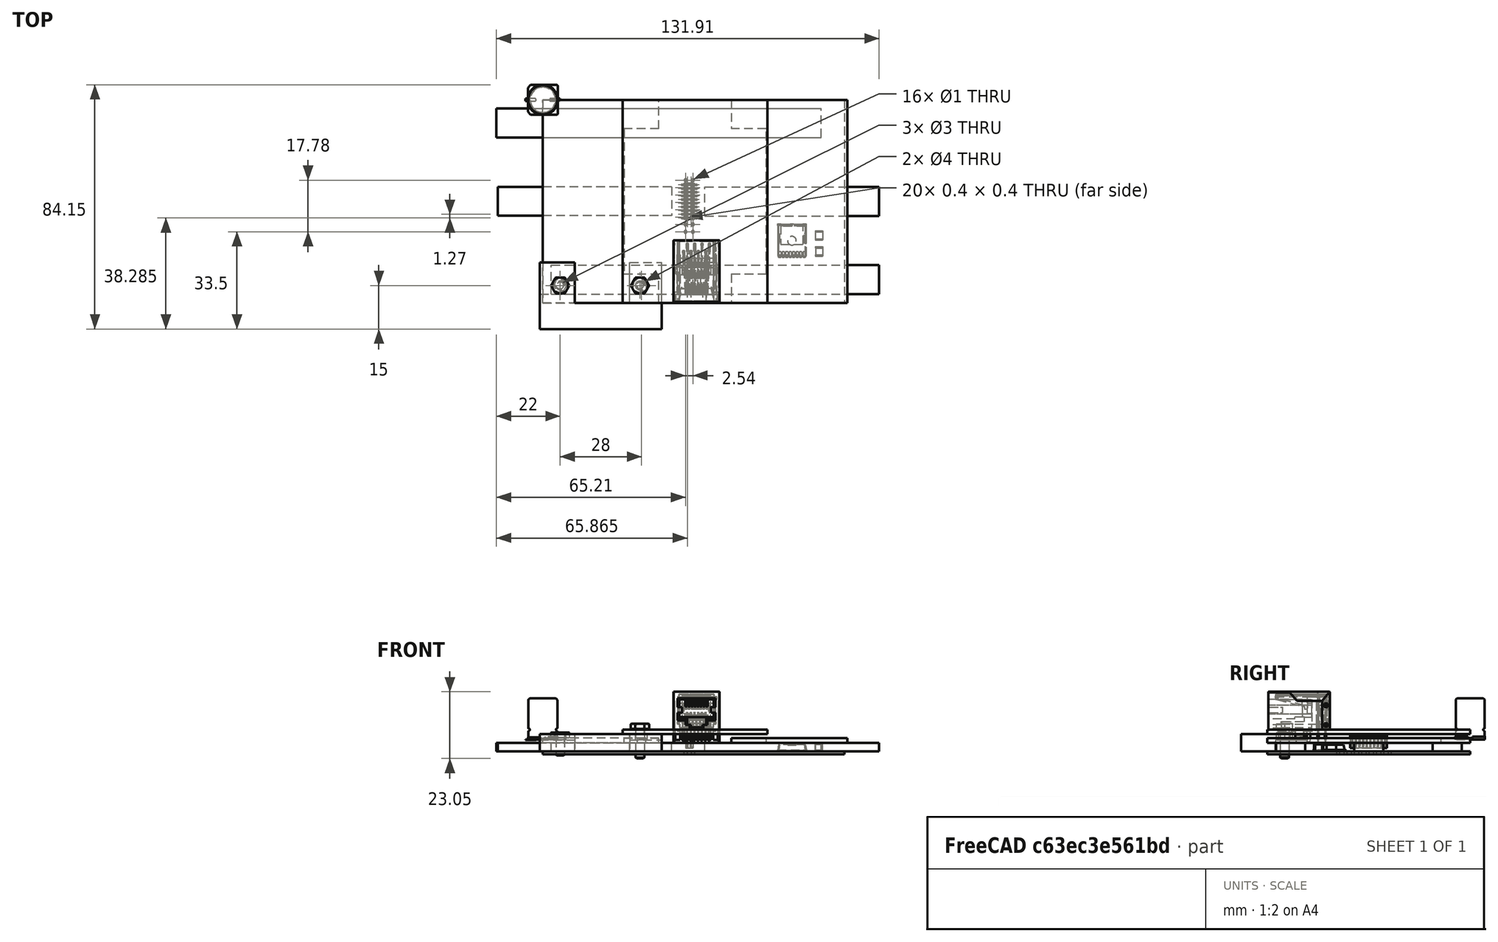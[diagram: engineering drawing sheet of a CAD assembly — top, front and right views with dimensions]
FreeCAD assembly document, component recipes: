
FREECAD ASSEMBLY — COMPONENT RECIPES ("Swiches")

This assembly document has 4 components, labeled P0..P3 below (a component is one placed body or linked part). 3 of them carry a construction recipe — the FreeCAD feature program that regenerates the part from scratch, quoted from this document or its linked companion documents; the rest are supplied as boundary geometry only. No exploded tour is included for this assembly.
COMPONENT P0 — geometry summary ("Switches"; no construction recipe available for this part):
  bounding box: 104.0 x 70.0 x 3.5 mm
  tessellated surface: 16,348 triangles
  volume: 10071 mm^3 (40% of its bounding box)
  symmetry: mirror-symmetric across its y mid-plane
COMPONENT P1 — recipe-attached ("Body", modeled in this document).
Construction recipe (the document's own serialized feature program — sketch geometry with constraints, then the solid features built on it; lengths are millimeters unless a unit is written):

FEATURE [Sketcher::SketchObject] Sketch
  FullyConstrained = true
  sketch-geometry (10):
    g0: LineSegment StartX=0 StartY=-70 StartZ=0 EndX=40 EndY=-70 EndZ=0
    g1: LineSegment StartX=40 StartY=-70 StartZ=0 EndX=40 EndY=-60 EndZ=0
    g2: LineSegment StartX=40 StartY=-10 StartZ=0 EndX=40 EndY=0 EndZ=0
    g3: LineSegment StartX=40 StartY=0 StartZ=0 EndX=0 EndY=0 EndZ=0
    g4: LineSegment StartX=40 StartY=-10 StartZ=0 EndX=28 EndY=-10 EndZ=0
    g5: LineSegment StartX=28 StartY=-60 StartZ=0 EndX=40 EndY=-60 EndZ=0
    g6: LineSegment StartX=0 StartY=0 StartZ=0 EndX=0 EndY=-70 EndZ=0
    g7: LineSegment StartX=28 StartY=-10 StartZ=0 EndX=28 EndY=-60 EndZ=0
    g8: Circle CenterX=6 CenterY=-64 CenterZ=0 NormalX=0 NormalY=0 NormalZ=1 AngleXU=0 Radius=1.5
    g9: Circle CenterX=34 CenterY=-64 CenterZ=0 NormalX=0 NormalY=0 NormalZ=1 AngleXU=0 Radius=1.5
  constraints (30):
    c: Coincident(g0,g1)
    c: Coincident(g5,g7)
    c: Coincident(g4,g7)
    c: Coincident(g4,g2)
    c: Coincident(g3,g2)
    c: Coincident(g6,g3)
    c: Coincident(g6,g0)
    c: Vertical(g6)
    c: Vertical(g7)
    c: Vertical(g1)
    c: Vertical(g2)
    c: Horizontal(g0)
    c: Horizontal(g3)
    c: Horizontal(g4)
    c: Horizontal(g5)
    c: Coincident(g1,g5)
    c: Equal(g4,g5)
    c: Equal(g2,g1)
    c: DistanceX(g3,g3) = 40
    c: DistanceY(g6,g6) = 70
    c: DistanceY(g2,g2) = 10
    c: DistanceX(g4,g4) = 12
    c: DistanceX(g3) = 0
    c: DistanceY(g3) = 0
    c: Diameter(g8) = 3
    c: DistanceY(g0,g8) = 6
    c: DistanceX(g0,g8) = 6
    c: DistanceY(g0,g9) = 6
    c: DistanceX(g9,g0) = 6
    c: Diameter(g9) = 3
FEATURE [PartDesign::Pad] Pad
  Direction = (1,1,1)
  Length = 1.6
  Length2 = 100
  Profile = -> Sketch
  Type = 0
FEATURE [PartDesign::Body] Body
  Group = -> [Sketch,Pad]
  Origin = -> Origin008
  Placement = pos=(0,0,3) rot=(0,0,1;0rad)
  Tip = -> Pad
COMPONENT P2 — recipe-attached ("Body001", modeled in this document).
Construction recipe (the document's own serialized feature program — sketch geometry with constraints, then the solid features built on it; lengths are millimeters unless a unit is written):

FEATURE [Sketcher::SketchObject] Sketch002
  FullyConstrained = true
  MapMode = 5
  Support = -> [XY_Plane009]
  sketch-geometry (5):
    g0: LineSegment StartX=10 StartY=0 StartZ=0 EndX=60 EndY=0 EndZ=0
    g1: LineSegment StartX=60 StartY=0 StartZ=0 EndX=60 EndY=-70 EndZ=0
    g2: LineSegment StartX=60 StartY=-70 StartZ=0 EndX=10 EndY=-70 EndZ=0
    g3: LineSegment StartX=10 StartY=-70 StartZ=0 EndX=10 EndY=0 EndZ=0
    g4: Circle CenterX=16 CenterY=-64 CenterZ=0 NormalX=0 NormalY=0 NormalZ=1 AngleXU=0 Radius=1.5
  constraints (15):
    c: Coincident(g0,g1)
    c: Coincident(g1,g2)
    c: Coincident(g2,g3)
    c: Coincident(g3,g0)
    c: Horizontal(g0)
    c: Horizontal(g2)
    c: Vertical(g1)
    c: Vertical(g3)
    c: Distance(g0) = 50
    c: Distance(g1) = 70
    c: DistanceX(g0,g-1) = -10
    c: DistanceY(g0,g-1) = 0
    c: DistanceY(g2,g4) = 6
    c: DistanceX(g2,g4) = 6
    c: Diameter(g4) = 3
FEATURE [PartDesign::Pad] Pad001
  Direction = (1,1,1)
  Length = 1.6
  Length2 = 100
  Profile = -> Sketch002
  Type = 0
FEATURE [PartDesign::Body] Body001
  Group = -> [Sketch002,Pad001]
  Origin = -> Origin009
  Placement = pos=(17.5,0,6) rot=(0,0,1;0rad)
  Tip = -> Pad001
COMPONENT P3 — recipe-attached ("Body002", modeled in this document).
Construction recipe (the document's own serialized feature program — sketch geometry with constraints, then the solid features built on it; lengths are millimeters unless a unit is written):

FEATURE [Sketcher::SketchObject] Sketch003
  FullyConstrained = true
  sketch-geometry (8):
    g0: LineSegment StartX=0 StartY=-70 StartZ=0 EndX=40 EndY=-70 EndZ=0
    g1: LineSegment StartX=40 StartY=-70 StartZ=0 EndX=40 EndY=-60 EndZ=0
    g2: LineSegment StartX=40 StartY=-10 StartZ=0 EndX=40 EndY=0 EndZ=0
    g3: LineSegment StartX=40 StartY=0 StartZ=0 EndX=0 EndY=0 EndZ=0
    g4: LineSegment StartX=40 StartY=-10 StartZ=0 EndX=28 EndY=-10 EndZ=0
    g5: LineSegment StartX=28 StartY=-60 StartZ=0 EndX=40 EndY=-60 EndZ=0
    g6: LineSegment StartX=0 StartY=0 StartZ=0 EndX=0 EndY=-70 EndZ=0
    g7: LineSegment StartX=28 StartY=-10 StartZ=0 EndX=28 EndY=-60 EndZ=0
  constraints (24):
    c: Coincident(g0,g1)
    c: Coincident(g5,g7)
    c: Coincident(g4,g7)
    c: Coincident(g4,g2)
    c: Coincident(g3,g2)
    c: Coincident(g6,g3)
    c: Coincident(g6,g0)
    c: Vertical(g6)
    c: Vertical(g7)
    c: Vertical(g1)
    c: Vertical(g2)
    c: Horizontal(g0)
    c: Horizontal(g3)
    c: Horizontal(g4)
    c: Horizontal(g5)
    c: Coincident(g1,g5)
    c: Equal(g4,g5)
    c: Equal(g2,g1)
    c: DistanceX(g3,g3) = 40
    c: DistanceY(g6,g6) = 70
    c: DistanceY(g2,g2) = 10
    c: DistanceX(g4,g4) = 12
    c: DistanceX(g3) = 0
    c: DistanceY(g3) = 0
FEATURE [PartDesign::Pad] Pad002
  Direction = (1,1,1)
  Length = 1.6
  Length2 = 100
  Profile = -> Sketch003
  Type = 0
FEATURE [PartDesign::Body] Body002
  Group = -> [Sketch003,Pad002]
  Origin = -> Origin010
  Placement = pos=(105,-70,3) rot=(0,0,1;3.14159rad)
  Tip = -> Pad002
PROVENANCE & LICENSES
A FreeCAD (.FCStd) document from a public repository crawl; recipes are the document's own serialized feature recipes (and, for linked parts, companion documents' recipes).
License: gpl-3.0.
